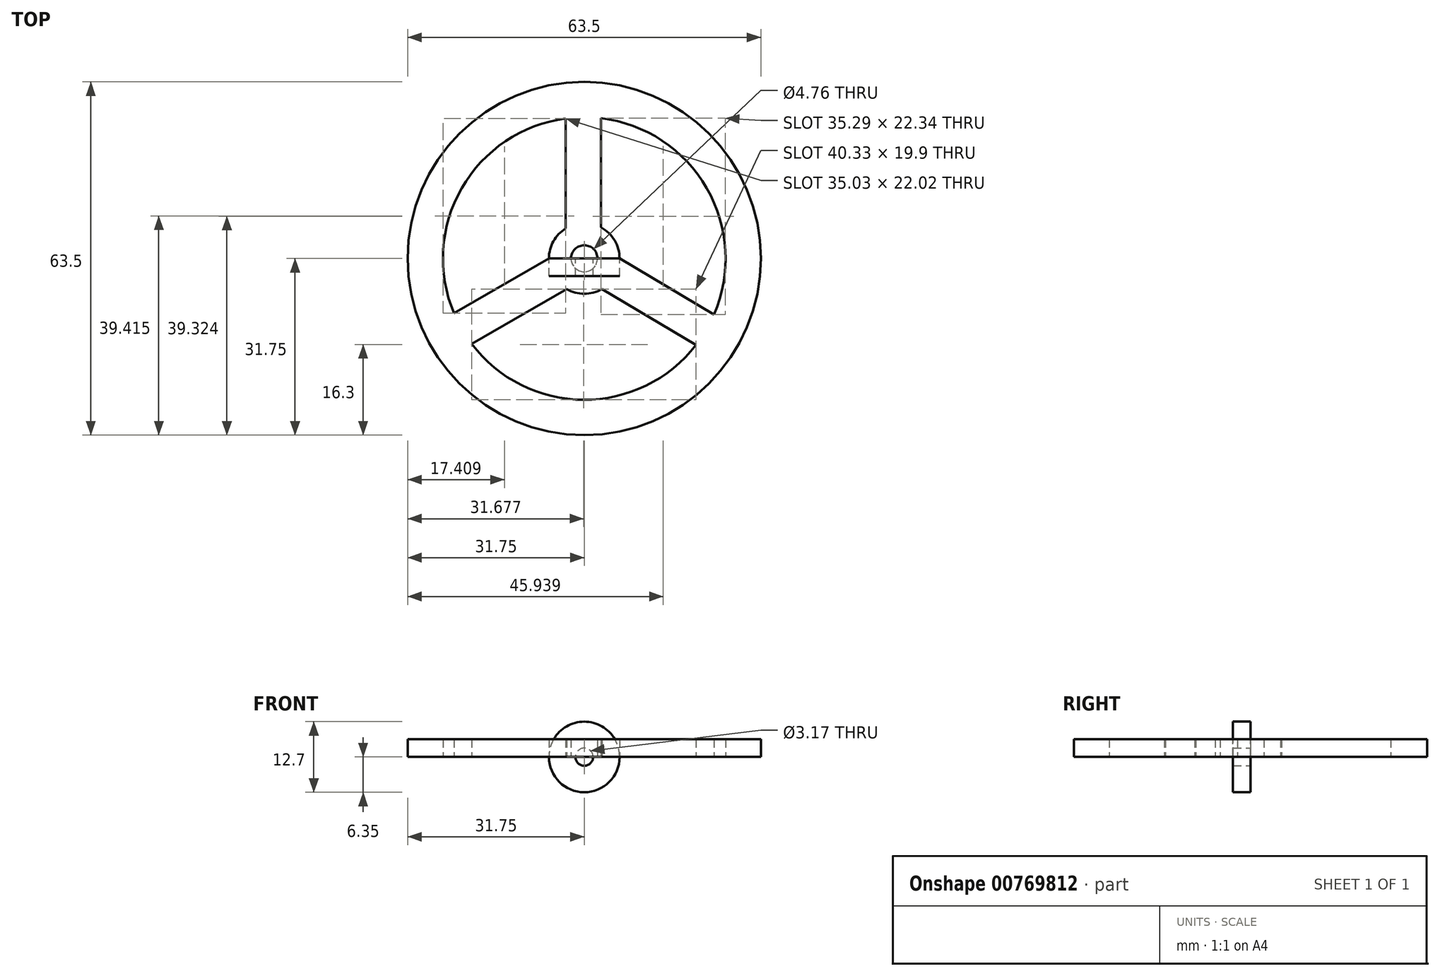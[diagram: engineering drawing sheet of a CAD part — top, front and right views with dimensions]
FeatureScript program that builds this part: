
annotation { "Feature Type Name" : "Feature", "Feature Type Description" : "" }
export const myFeature = defineFeature(function(context is Context, id is Id, definition is map)
    precondition{}
    {
        {
            var Q0;
            Q0=qCreatedBy(makeId("Top.planeOp"),FACE);
            var sketch = newSketch(context, id + "F0", { "sketchPlane" : qUnion([Q0])});
            skCircle(sketch, "E0", {"center": v(0, 0) * mm, "radius": 31.75 * mm});
            skCircle(sketch, "E1", {"center": v(0, 0) * mm, "radius": 2.38 * mm});
            skArc(sketch, "E2", {"start": v(-20.24, -15.35) * mm, "mid": v(-0.12, -25.4) * mm, "end": v(20.1, -15.54) * mm});
            skArc(sketch, "E3", {"start": v(-3.33, 5.4) * mm, "mid": v(-5.54, 3.1) * mm, "end": v(-6.35, 0) * mm});
            skLineSegment(sketch, "E4", {"start": v(3.17, -5.5) * mm, "end": v(20.1, -15.54) * mm});
            skLineSegment(sketch, "E5", {"start": v(3.02, 25.22) * mm, "end": v(3.02, 5.59) * mm});
            skLineSegment(sketch, "E6", {"start": v(-3.33, 25.18) * mm, "end": v(-3.33, 5.4) * mm});
            skLineSegment(sketch, "E7", {"start": v(-6.35, 0) * mm, "end": v(-23.41, -9.85) * mm});
            skLineSegment(sketch, "E8", {"start": v(-3.17, -5.5) * mm, "end": v(-20.24, -15.35) * mm});
            skLineSegment(sketch, "E9", {"start": v(6.35, 0) * mm, "end": v(23.32, -10.07) * mm});
            skArc(sketch, "E10.trimOffspring", {"start": v(23.32, -10.07) * mm, "mid": v(22.02, 12.66) * mm, "end": v(3.02, 25.22) * mm});
            skArc(sketch, "E11.trimOffspring", {"start": v(-3.33, 25.18) * mm, "mid": v(-22.04, 12.63) * mm, "end": v(-23.41, -9.85) * mm});
            skArc(sketch, "E12.trimOffspring", {"start": v(6.35, 0) * mm, "mid": v(5.45, 3.25) * mm, "end": v(3.02, 5.59) * mm});
            skArc(sketch, "E13.trimOffspring", {"start": v(-3.18, -5.5) * mm, "mid": v(0, -6.35) * mm, "end": v(3.17, -5.5) * mm});
            skSolve(sketch);
        }
        {
            var Q0;
            Q0=makeQuery(id+"F0.imprint","IMPRINT",FACE,{"disambiguationData":[TD([[makeQuery(id+"F0.imprint","IMPRINT",EDGE,{"derivedFrom":sQuery(id+"F0.wireOp",EDGE,"E0")}),1.0]])]});
            extrude(context, id + "F1", {"entities" : qUnion([Q0]), "depth" : 3.17 * mm, "offsetDistance" : 25.4 * mm});
        }
        {
            var Q0;
            Q0=qCreatedBy(makeId("Front.planeOp"),FACE);
            var sketch = newSketch(context, id + "F2", { "sketchPlane" : qUnion([Q0])});
            skCircle(sketch, "E14", {"center": v(0, 0) * mm, "radius": 6.35 * mm});
            skCircle(sketch, "E15", {"center": v(0, 0) * mm, "radius": 1.59 * mm});
            skSolve(sketch);
        }
        {
            var Q0;
            Q0=makeQuery(id+"F2.imprint","IMPRINT",FACE,{"disambiguationData":[TD([[makeQuery(id+"F2.imprint","IMPRINT",EDGE,{"derivedFrom":sQuery(id+"F2.wireOp",EDGE,"E14")}),1.0]])]});
            extrude(context, id + "F3", {"entities" : qUnion([Q0]), "depth" : 3.17 * mm, "offsetDistance" : 25.4 * mm});
        }
    });
